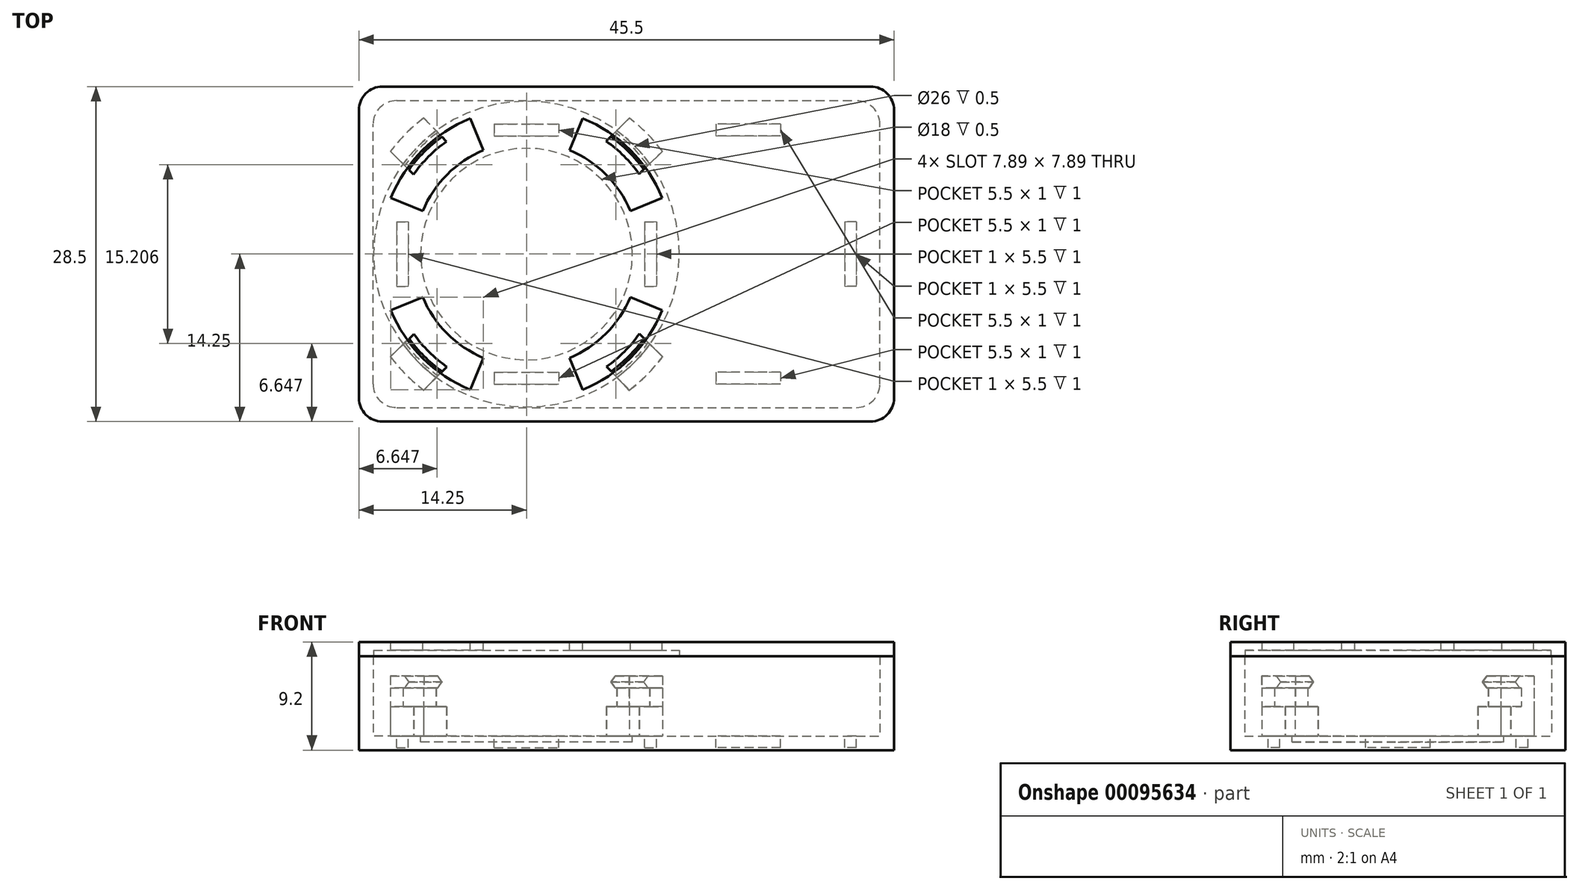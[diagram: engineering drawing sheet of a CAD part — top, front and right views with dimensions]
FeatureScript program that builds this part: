
annotation { "Feature Type Name" : "Feature", "Feature Type Description" : "" }
export const myFeature = defineFeature(function(context is Context, id is Id, definition is map)
    precondition{}
    {
        {
            var Q0;
            Q0=qCreatedBy(makeId("Top.planeOp"),FACE);
            var sketch = newSketch(context, id + "F0", { "sketchPlane" : qUnion([Q0])});
            skLineSegment(sketch, "E0.bottom", {"start": v(0, 0) * mm, "end": v(45.5, 0) * mm});
            skLineSegment(sketch, "E0.top", {"start": v(0, 28.5) * mm, "end": v(45.5, 28.5) * mm});
            skLineSegment(sketch, "E0.left", {"start": v(0, 0) * mm, "end": v(0, 28.5) * mm});
            skLineSegment(sketch, "E0.right", {"start": v(45.5, 0) * mm, "end": v(45.5, 28.5) * mm});
            skSolve(sketch);
        }
        {
            var Q0;
            Q0=qSketchRegion(id+"F0",true);
            extrude(context, id + "F1", {"entities" : qUnion([Q0]), "depth" : 8 * mm});
        }
        {
            var Q0;
            Q0=makeQuery(id+"F1.opExtrude","CAP_FACE",FACE,{"disambiguationData":[OSD([sQuery(id+"F0.wireOp",EDGE,"E0.bottom"),sQuery(id+"F0.wireOp",EDGE,"E0.top"),sQuery(id+"F0.wireOp",EDGE,"E0.left"),sQuery(id+"F0.wireOp",EDGE,"E0.right")])],"isStart":false});
            shell(context, id + "F2", {"entities" : qUnion([Q0]), "thickness" : 1.2 * mm});
        }
        {
            var Q0;
            Q0=makeQuery(id+"F2.opShell","OFFSET_EDGE",EDGE,{"disambiguationData":[OSD([sQuery(id+"F0.wireOp",EDGE,"E0.top"),sQuery(id+"F0.wireOp",EDGE,"E0.right")])]});
            var Q1;
            Q1=makeQuery(id+"F2.opShell","OFFSET_EDGE",EDGE,{"disambiguationData":[OSD([sQuery(id+"F0.wireOp",EDGE,"E0.top"),sQuery(id+"F0.wireOp",EDGE,"E0.left")])]});
            var Q2;
            Q2=makeQuery(id+"F2.opShell","OFFSET_EDGE",EDGE,{"disambiguationData":[OSD([sQuery(id+"F0.wireOp",EDGE,"E0.bottom"),sQuery(id+"F0.wireOp",EDGE,"E0.left")])]});
            var Q3;
            Q3=makeQuery(id+"F1.opExtrude","SWEPT_EDGE",EDGE,{"disambiguationData":[OSD([sQuery(id+"F0.wireOp",EDGE,"E0.top"),sQuery(id+"F0.wireOp",EDGE,"E0.right")])]});
            var Q4;
            Q4=makeQuery(id+"F1.opExtrude","SWEPT_EDGE",EDGE,{"disambiguationData":[OSD([sQuery(id+"F0.wireOp",EDGE,"E0.bottom"),sQuery(id+"F0.wireOp",EDGE,"E0.right")])]});
            var Q5;
            Q5=makeQuery(id+"F1.opExtrude","SWEPT_EDGE",EDGE,{"disambiguationData":[OSD([sQuery(id+"F0.wireOp",EDGE,"E0.top"),sQuery(id+"F0.wireOp",EDGE,"E0.left")])]});
            var Q6;
            Q6=makeQuery(id+"F1.opExtrude","SWEPT_EDGE",EDGE,{"disambiguationData":[OSD([sQuery(id+"F0.wireOp",EDGE,"E0.bottom"),sQuery(id+"F0.wireOp",EDGE,"E0.left")])]});
            var Q7;
            Q7=makeQuery(id+"F2.opShell","OFFSET_EDGE",EDGE,{"disambiguationData":[OSD([sQuery(id+"F0.wireOp",EDGE,"E0.bottom"),sQuery(id+"F0.wireOp",EDGE,"E0.right")])]});
            fillet(context, id + "F3", {"entities" : qUnion([Q0, Q1, Q2, Q3, Q4, Q5, Q6, Q7]), "radius" : 2 * mm, "tangentPropagation" : true, "allowEdgeOverflow" : false});
        }
        {
            var Q0;
            Q0=makeQuery(id+"F1.opExtrude","CAP_FACE",FACE,{"disambiguationData":[OSD([sQuery(id+"F0.wireOp",EDGE,"E0.bottom"),sQuery(id+"F0.wireOp",EDGE,"E0.top"),sQuery(id+"F0.wireOp",EDGE,"E0.left"),sQuery(id+"F0.wireOp",EDGE,"E0.right")])],"isStart":false});
            var sketch = newSketch(context, id + "F4", { "sketchPlane" : qUnion([Q0])});
            skArc(sketch, "E1.0", {"start": v(45.5, 26.5) * mm, "mid": v(44.91, 27.91) * mm, "end": v(43.5, 28.5) * mm});
            skLineSegment(sketch, "E1.1", {"start": v(45.5, 2) * mm, "end": v(45.5, 26.5) * mm});
            skLineSegment(sketch, "E2.0", {"start": v(2, 28.5) * mm, "end": v(43.5, 28.5) * mm});
            skArc(sketch, "E2.1", {"start": v(2, 28.5) * mm, "mid": v(0.59, 27.91) * mm, "end": v(0, 26.5) * mm});
            skArc(sketch, "E2.4", {"start": v(0, 2) * mm, "mid": v(0.59, 0.59) * mm, "end": v(2, 0) * mm});
            skLineSegment(sketch, "E2.5", {"start": v(0, 2) * mm, "end": v(0, 26.5) * mm});
            skArc(sketch, "E3.0", {"start": v(43.5, 0) * mm, "mid": v(44.91, 0.59) * mm, "end": v(45.5, 2) * mm});
            skLineSegment(sketch, "E4", {"start": v(2, 0) * mm, "end": v(43.5, 0) * mm});
            skSolve(sketch);
        }
        {
            var Q0;
            Q0=qSketchRegion(id+"F4",true);
            extrude(context, id + "F5", {"entities" : qUnion([Q0]), "depth" : 1.2 * mm});
        }
        {
            var Q0;
            Q0=makeQuery(id+"F2.opShell","OFFSET_FACE",FACE,{"disambiguationData":[OSD([sQuery(id+"F0.wireOp",EDGE,"E0.bottom"),sQuery(id+"F0.wireOp",EDGE,"E0.top"),sQuery(id+"F0.wireOp",EDGE,"E0.left"),sQuery(id+"F0.wireOp",EDGE,"E0.right")])]});
            var sketch = newSketch(context, id + "F6", { "sketchPlane" : qUnion([Q0])});
            skLineSegment(sketch, "E5.bottom", {"start": v(3.2, 17) * mm, "end": v(4.2, 17) * mm});
            skLineSegment(sketch, "E5.top", {"start": v(3.2, 11.5) * mm, "end": v(4.2, 11.5) * mm});
            skLineSegment(sketch, "E5.left", {"start": v(3.2, 17) * mm, "end": v(3.2, 11.5) * mm});
            skLineSegment(sketch, "E5.right", {"start": v(4.2, 17) * mm, "end": v(4.2, 11.5) * mm});
            skLineSegment(sketch, "E6.bottom", {"start": v(11.5, 25.3) * mm, "end": v(17, 25.3) * mm});
            skLineSegment(sketch, "E6.top", {"start": v(11.5, 24.3) * mm, "end": v(17, 24.3) * mm});
            skLineSegment(sketch, "E6.left", {"start": v(11.5, 25.3) * mm, "end": v(11.5, 24.3) * mm});
            skLineSegment(sketch, "E6.right", {"start": v(17, 25.3) * mm, "end": v(17, 24.3) * mm});
            skLineSegment(sketch, "E7.bottom", {"start": v(11.5, 3.2) * mm, "end": v(17, 3.2) * mm});
            skLineSegment(sketch, "E7.top", {"start": v(11.5, 4.2) * mm, "end": v(17, 4.2) * mm});
            skLineSegment(sketch, "E7.left", {"start": v(11.5, 4.2) * mm, "end": v(11.5, 3.2) * mm});
            skLineSegment(sketch, "E7.right", {"start": v(17, 4.2) * mm, "end": v(17, 3.2) * mm});
            skLineSegment(sketch, "E8.bottom", {"start": v(24.3, 17) * mm, "end": v(25.3, 17) * mm});
            skLineSegment(sketch, "E8.top", {"start": v(24.3, 11.5) * mm, "end": v(25.3, 11.5) * mm});
            skLineSegment(sketch, "E8.left", {"start": v(24.3, 17) * mm, "end": v(24.3, 11.5) * mm});
            skLineSegment(sketch, "E8.right", {"start": v(25.3, 17) * mm, "end": v(25.3, 11.5) * mm});
            skLineSegment(sketch, "E9", {"start": v(14.25, 32.06) * mm, "end": v(14.25, -4.11) * mm, "construction": true});
            skLineSegment(sketch, "E10", {"start": v(0, 14.25) * mm, "end": v(45.5, 14.25) * mm, "construction": true});
            skLineSegment(sketch, "E11", {"start": v(45.5, 14.25) * mm, "end": v(53.48, 14.25) * mm, "construction": true});
            skLineSegment(sketch, "E12.MirrorCS", {"start": v(42.3, 17) * mm, "end": v(41.3, 17) * mm});
            skLineSegment(sketch, "E13.MirrorCS", {"start": v(42.3, 11.5) * mm, "end": v(41.3, 11.5) * mm});
            skLineSegment(sketch, "E14.MirrorCS", {"start": v(30.35, 25.3) * mm, "end": v(30.35, 24.3) * mm});
            skLineSegment(sketch, "E15.MirrorCS", {"start": v(35.85, 4.2) * mm, "end": v(35.85, 3.2) * mm});
            skLineSegment(sketch, "E16.MirrorCS", {"start": v(30.35, 4.2) * mm, "end": v(30.35, 3.2) * mm});
            skLineSegment(sketch, "E17.MirrorCS", {"start": v(35.85, 25.3) * mm, "end": v(35.85, 24.3) * mm});
            skLineSegment(sketch, "E18.MirrorCS", {"start": v(42.3, 17) * mm, "end": v(42.3, 11.5) * mm});
            skLineSegment(sketch, "E19.MirrorCS", {"start": v(41.3, 17) * mm, "end": v(41.3, 11.5) * mm});
            skLineSegment(sketch, "E20.MirrorCS", {"start": v(35.85, 25.3) * mm, "end": v(30.35, 25.3) * mm});
            skLineSegment(sketch, "E21.MirrorCS", {"start": v(35.85, 24.3) * mm, "end": v(30.35, 24.3) * mm});
            skLineSegment(sketch, "E22.MirrorCS", {"start": v(35.85, 4.2) * mm, "end": v(30.35, 4.2) * mm});
            skLineSegment(sketch, "E23.MirrorCS", {"start": v(35.85, 3.2) * mm, "end": v(30.35, 3.2) * mm});
            skSolve(sketch);
        }
        {
            var Q0;
            Q0=qSketchRegion(id+"F6",true);
            extrude(context, id + "F7", {"entities" : qUnion([Q0]), "operationType" : NewBodyOperationType.REMOVE, "oppositeDirection" : true, "depth" : 1 * mm});
        }
        {
            var Q0;
            Q0=makeQuery(id+"F2.opShell","OFFSET_FACE",FACE,{"disambiguationData":[OSD([sQuery(id+"F0.wireOp",EDGE,"E0.bottom"),sQuery(id+"F0.wireOp",EDGE,"E0.top"),sQuery(id+"F0.wireOp",EDGE,"E0.left"),sQuery(id+"F0.wireOp",EDGE,"E0.right")])]});
            var sketch = newSketch(context, id + "F8", { "sketchPlane" : qUnion([Q0])});
            skCircle(sketch, "E24", {"center": v(14.25, 14.25) * mm, "radius": 12.85 * mm, "construction": true});
            skLineSegment(sketch, "E25", {"start": v(14.25, 31.13) * mm, "end": v(14.25, -1.74) * mm, "construction": true});
            skLineSegment(sketch, "E26", {"start": v(14.25, 14.25) * mm, "end": v(3.2, 25.3) * mm, "construction": true});
            skLineSegment(sketch, "E27", {"start": v(4.65, 21.03) * mm, "end": v(2.68, 23) * mm});
            skLineSegment(sketch, "E28", {"start": v(5.51, 25.82) * mm, "end": v(7.44, 23.82) * mm});
            skArc(sketch, "E29.trimOffspring", {"start": v(7.44, 23.82) * mm, "mid": v(5.93, 22.54) * mm, "end": v(4.65, 21.03) * mm});
            skArc(sketch, "E30.trimOffspring", {"start": v(5.51, 25.82) * mm, "mid": v(4, 24.5) * mm, "end": v(2.68, 23) * mm});
            skLineSegment(sketch, "E31.1.0", {"start": v(2.68, 5.51) * mm, "end": v(4.68, 7.44) * mm});
            skArc(sketch, "E31.1.1", {"start": v(2.68, 5.51) * mm, "mid": v(4, 4) * mm, "end": v(5.5, 2.68) * mm});
            skLineSegment(sketch, "E31.1.2", {"start": v(7.47, 4.65) * mm, "end": v(5.5, 2.68) * mm});
            skArc(sketch, "E31.1.3", {"start": v(4.68, 7.44) * mm, "mid": v(5.96, 5.93) * mm, "end": v(7.47, 4.65) * mm});
            skLineSegment(sketch, "E31.2.0", {"start": v(22.99, 2.68) * mm, "end": v(21.06, 4.68) * mm});
            skArc(sketch, "E31.2.1", {"start": v(22.99, 2.68) * mm, "mid": v(24.5, 4) * mm, "end": v(25.82, 5.5) * mm});
            skLineSegment(sketch, "E31.2.2", {"start": v(23.85, 7.47) * mm, "end": v(25.82, 5.5) * mm});
            skArc(sketch, "E31.2.3", {"start": v(21.06, 4.68) * mm, "mid": v(22.57, 5.96) * mm, "end": v(23.85, 7.47) * mm});
            skLineSegment(sketch, "E31.3.0", {"start": v(25.82, 22.99) * mm, "end": v(23.82, 21.06) * mm});
            skArc(sketch, "E31.3.1", {"start": v(25.82, 22.99) * mm, "mid": v(24.5, 24.5) * mm, "end": v(23, 25.82) * mm});
            skLineSegment(sketch, "E31.3.2", {"start": v(21.03, 23.85) * mm, "end": v(23, 25.82) * mm});
            skArc(sketch, "E31.3.3", {"start": v(23.82, 21.06) * mm, "mid": v(22.54, 22.57) * mm, "end": v(21.03, 23.85) * mm});
            skSolve(sketch);
        }
        {
            var Q0;
            Q0=qSketchRegion(id+"F8",true);
            extrude(context, id + "F9", {"entities" : qUnion([Q0]), "operationType" : NewBodyOperationType.ADD, "depth" : 2.5 * mm});
        }
        {
            var Q0;
            Q0=makeQuery(id+"F9.opExtrude","CAP_FACE",FACE,{"disambiguationData":[OSD([sQuery(id+"F8.wireOp",EDGE,"E27"),sQuery(id+"F8.wireOp",EDGE,"E28"),sQuery(id+"F8.wireOp",EDGE,"E29.trimOffspring"),sQuery(id+"F8.wireOp",EDGE,"E30.trimOffspring")])],"isStart":false});
            var sketch = newSketch(context, id + "F10", { "sketchPlane" : qUnion([Q0])});
            skArc(sketch, "E32", {"start": v(3.75, 6.58) * mm, "mid": v(5.06, 5.06) * mm, "end": v(6.58, 3.75) * mm});
            skArc(sketch, "E33", {"start": v(5.51, 25.82) * mm, "mid": v(4, 24.5) * mm, "end": v(2.68, 23) * mm});
            skLineSegment(sketch, "E34", {"start": v(6.56, 24.73) * mm, "end": v(5.51, 25.82) * mm});
            skLineSegment(sketch, "E35", {"start": v(3.75, 21.92) * mm, "end": v(2.68, 23) * mm});
            skLineSegment(sketch, "E36", {"start": v(22.99, 25.82) * mm, "end": v(21.92, 24.75) * mm});
            skLineSegment(sketch, "E37", {"start": v(24.72, 21.96) * mm, "end": v(25.82, 22.99) * mm});
            skLineSegment(sketch, "E38", {"start": v(24.75, 6.58) * mm, "end": v(25.82, 5.51) * mm});
            skLineSegment(sketch, "E39", {"start": v(21.94, 3.77) * mm, "end": v(22.98, 2.67) * mm});
            skLineSegment(sketch, "E40", {"start": v(3.75, 6.58) * mm, "end": v(2.67, 5.52) * mm});
            skLineSegment(sketch, "E41", {"start": v(5.5, 2.68) * mm, "end": v(6.58, 3.75) * mm});
            skArc(sketch, "E42.trimOffspring", {"start": v(6.56, 24.73) * mm, "mid": v(5.05, 23.43) * mm, "end": v(3.75, 21.92) * mm});
            skArc(sketch, "E43.trimOffspring", {"start": v(2.67, 5.52) * mm, "mid": v(3.99, 4) * mm, "end": v(5.5, 2.68) * mm});
            skArc(sketch, "E44.trimOffspring", {"start": v(22.98, 2.67) * mm, "mid": v(24.5, 4) * mm, "end": v(25.82, 5.51) * mm});
            skArc(sketch, "E45.trimOffspring", {"start": v(25.82, 22.99) * mm, "mid": v(24.5, 24.5) * mm, "end": v(22.99, 25.82) * mm});
            skArc(sketch, "E46.trimOffspring", {"start": v(24.72, 21.96) * mm, "mid": v(23.43, 23.46) * mm, "end": v(21.92, 24.75) * mm});
            skArc(sketch, "E47.trimOffspring", {"start": v(21.94, 3.77) * mm, "mid": v(23.45, 5.07) * mm, "end": v(24.75, 6.58) * mm});
            skSolve(sketch);
        }
        {
            var Q0;
            Q0=qSketchRegion(id+"F10",true);
            extrude(context, id + "F11", {"entities" : qUnion([Q0]), "operationType" : NewBodyOperationType.ADD, "depth" : 1.6 * mm});
        }
        {
            var Q0;
            Q0=makeQuery(id+"F11.opExtrude","CAP_FACE",FACE,{"disambiguationData":[OSD([sQuery(id+"F10.wireOp",EDGE,"E36"),sQuery(id+"F10.wireOp",EDGE,"E37"),sQuery(id+"F10.wireOp",EDGE,"E45.trimOffspring"),sQuery(id+"F10.wireOp",EDGE,"E46.trimOffspring")])],"isStart":false});
            var sketch = newSketch(context, id + "F12", { "sketchPlane" : qUnion([Q0])});
            skArc(sketch, "E48", {"start": v(7.05, 24.23) * mm, "mid": v(5.54, 22.93) * mm, "end": v(4.25, 21.42) * mm});
            skArc(sketch, "E49", {"start": v(5.52, 25.82) * mm, "mid": v(4, 24.5) * mm, "end": v(2.68, 22.99) * mm});
            skLineSegment(sketch, "E50", {"start": v(22.99, 25.82) * mm, "end": v(21.42, 24.24) * mm});
            skLineSegment(sketch, "E51", {"start": v(25.82, 22.99) * mm, "end": v(24.2, 21.47) * mm});
            skLineSegment(sketch, "E52", {"start": v(24.2, 21.47) * mm, "end": v(24.19, 21.46) * mm});
            skLineSegment(sketch, "E53", {"start": v(5.52, 25.82) * mm, "end": v(7.05, 24.23) * mm});
            skLineSegment(sketch, "E54", {"start": v(2.68, 22.99) * mm, "end": v(4.25, 21.42) * mm});
            skLineSegment(sketch, "E55", {"start": v(2.67, 5.53) * mm, "end": v(4.25, 7.08) * mm});
            skLineSegment(sketch, "E56", {"start": v(5.52, 2.67) * mm, "end": v(7.04, 4.28) * mm});
            skLineSegment(sketch, "E57", {"start": v(25.83, 5.53) * mm, "end": v(24.22, 7.05) * mm});
            skLineSegment(sketch, "E58", {"start": v(22.96, 2.66) * mm, "end": v(21.45, 4.28) * mm});
            skArc(sketch, "E59.trimOffspring", {"start": v(4.25, 7.08) * mm, "mid": v(5.53, 5.57) * mm, "end": v(7.04, 4.28) * mm});
            skArc(sketch, "E60.trimOffspring", {"start": v(2.67, 5.53) * mm, "mid": v(4, 4) * mm, "end": v(5.52, 2.67) * mm});
            skArc(sketch, "E61.trimOffspring", {"start": v(24.2, 21.47) * mm, "mid": v(22.92, 22.97) * mm, "end": v(21.42, 24.24) * mm});
            skArc(sketch, "E62.trimOffspring", {"start": v(25.82, 22.99) * mm, "mid": v(24.5, 24.5) * mm, "end": v(22.99, 25.82) * mm});
            skArc(sketch, "E63.trimOffspring", {"start": v(21.45, 4.28) * mm, "mid": v(22.95, 5.55) * mm, "end": v(24.22, 7.05) * mm});
            skArc(sketch, "E64.trimOffspring", {"start": v(22.96, 2.66) * mm, "mid": v(24.5, 4) * mm, "end": v(25.83, 5.53) * mm});
            skSolve(sketch);
        }
        {
            var Q0;
            Q0=qSketchRegion(id+"F12",true);
            extrude(context, id + "F13", {"entities" : qUnion([Q0]), "operationType" : NewBodyOperationType.ADD, "depth" : 1 * mm});
        }
        {
            var Q0;
            Q0=makeQuery(id+"F13.opExtrude","CAP_EDGE",EDGE,{"disambiguationData":[OSD([sQuery(id+"F12.wireOp",EDGE,"E59.trimOffspring")])],"isStart":false});
            var Q1;
            Q1=makeQuery(id+"F13.opExtrude","CAP_EDGE",EDGE,{"disambiguationData":[OSD([sQuery(id+"F12.wireOp",EDGE,"E59.trimOffspring")])],"isStart":true});
            var Q2;
            Q2=makeQuery(id+"F13.opExtrude","CAP_EDGE",EDGE,{"disambiguationData":[OSD([sQuery(id+"F12.wireOp",EDGE,"E48")])],"isStart":false});
            var Q3;
            Q3=makeQuery(id+"F13.opExtrude","CAP_EDGE",EDGE,{"disambiguationData":[OSD([sQuery(id+"F12.wireOp",EDGE,"E48")])],"isStart":true});
            var Q4;
            Q4=makeQuery(id+"F13.opExtrude","CAP_EDGE",EDGE,{"disambiguationData":[OSD([sQuery(id+"F12.wireOp",EDGE,"E61.trimOffspring")])],"isStart":false});
            var Q5;
            Q5=makeQuery(id+"F13.opExtrude","CAP_EDGE",EDGE,{"disambiguationData":[OSD([sQuery(id+"F12.wireOp",EDGE,"E63.trimOffspring")])],"isStart":false});
            var Q6;
            Q6=makeQuery(id+"F13.opExtrude","CAP_EDGE",EDGE,{"disambiguationData":[OSD([sQuery(id+"F12.wireOp",EDGE,"E63.trimOffspring")])],"isStart":true});
            var Q7;
            Q7=makeQuery(id+"F13.opExtrude","CAP_EDGE",EDGE,{"disambiguationData":[OSD([sQuery(id+"F12.wireOp",EDGE,"E61.trimOffspring")])],"isStart":true});
            chamfer(context, id + "F14", {"entities" : qUnion([Q0, Q1, Q2, Q3, Q4, Q5, Q6, Q7]), "width" : .5 * mm, "tangentPropagation" : true});
        }
        {
            var Q0;
            Q0=makeQuery(id+"F2.opShell","OFFSET_FACE",FACE,{"disambiguationData":[OSD([sQuery(id+"F0.wireOp",EDGE,"E0.bottom"),sQuery(id+"F0.wireOp",EDGE,"E0.top"),sQuery(id+"F0.wireOp",EDGE,"E0.left"),sQuery(id+"F0.wireOp",EDGE,"E0.right")])]});
            var sketch = newSketch(context, id + "F15", { "sketchPlane" : qUnion([Q0])});
            skCircle(sketch, "E65", {"center": v(14.25, 14.25) * mm, "radius": 9 * mm});
            skSolve(sketch);
        }
        {
            var Q0;
            Q0=qSketchRegion(id+"F15",true);
            extrude(context, id + "F16", {"entities" : qUnion([Q0]), "operationType" : NewBodyOperationType.REMOVE, "oppositeDirection" : true, "depth" : .5 * mm});
        }
        {
            var Q0;
            Q0=makeQuery(id+"F5.opExtrude","CAP_FACE",FACE,{"disambiguationData":[OSD([sQuery(id+"F4.wireOp",EDGE,"E1.0"),sQuery(id+"F4.wireOp",EDGE,"E1.1"),sQuery(id+"F4.wireOp",EDGE,"E2.0"),sQuery(id+"F4.wireOp",EDGE,"E2.1"),sQuery(id+"F4.wireOp",EDGE,"E2.4"),sQuery(id+"F4.wireOp",EDGE,"E2.5"),sQuery(id+"F4.wireOp",EDGE,"E3.0"),sQuery(id+"F4.wireOp",EDGE,"E4")])],"isStart":false});
            var sketch = newSketch(context, id + "F17", { "sketchPlane" : qUnion([Q0])});
            skArc(sketch, "E66", {"start": v(2.7, 9.47) * mm, "mid": v(5.41, 5.41) * mm, "end": v(9.47, 2.7) * mm});
            skArc(sketch, "E67", {"start": v(5.42, 10.6) * mm, "mid": v(7.5, 7.5) * mm, "end": v(10.6, 5.42) * mm});
            skLineSegment(sketch, "E68", {"start": v(17.9, 23.08) * mm, "end": v(19.03, 25.8) * mm});
            skLineSegment(sketch, "E69", {"start": v(23.08, 17.9) * mm, "end": v(25.8, 19.03) * mm});
            skLineSegment(sketch, "E70", {"start": v(14.25, 14.25) * mm, "end": v(27.9, 27.9) * mm, "construction": true});
            skLineSegment(sketch, "E71", {"start": v(14.25, 14.25) * mm, "end": v(14.25, 29.28) * mm, "construction": true});
            skLineSegment(sketch, "E72", {"start": v(14.25, 14.25) * mm, "end": v(1.2, 27.3) * mm, "construction": true});
            skLineSegment(sketch, "E73", {"start": v(14.25, 14.25) * mm, "end": v(6, 6) * mm, "construction": true});
            skLineSegment(sketch, "E74", {"start": v(14.25, 14.25) * mm, "end": v(24.15, 4.35) * mm, "construction": true});
            skLineSegment(sketch, "E75", {"start": v(10.6, 23.08) * mm, "end": v(9.47, 25.8) * mm});
            skLineSegment(sketch, "E76", {"start": v(5.42, 17.9) * mm, "end": v(2.7, 19.03) * mm});
            skLineSegment(sketch, "E77", {"start": v(5.42, 10.6) * mm, "end": v(2.7, 9.47) * mm});
            skLineSegment(sketch, "E78", {"start": v(10.6, 5.42) * mm, "end": v(9.47, 2.7) * mm});
            skLineSegment(sketch, "E79", {"start": v(17.9, 5.42) * mm, "end": v(19.03, 2.7) * mm});
            skLineSegment(sketch, "E80", {"start": v(23.08, 10.6) * mm, "end": v(25.8, 9.47) * mm});
            skArc(sketch, "E81.trimOffspring", {"start": v(23.08, 17.9) * mm, "mid": v(21, 21) * mm, "end": v(17.9, 23.08) * mm});
            skArc(sketch, "E82.trimOffspring", {"start": v(25.8, 19.03) * mm, "mid": v(23.09, 23.09) * mm, "end": v(19.03, 25.8) * mm});
            skArc(sketch, "E83.trimOffspring", {"start": v(10.6, 23.08) * mm, "mid": v(7.5, 21) * mm, "end": v(5.42, 17.9) * mm});
            skArc(sketch, "E84.trimOffspring", {"start": v(9.47, 25.8) * mm, "mid": v(5.41, 23.09) * mm, "end": v(2.7, 19.03) * mm});
            skArc(sketch, "E85.trimOffspring", {"start": v(17.9, 5.42) * mm, "mid": v(21, 7.5) * mm, "end": v(23.08, 10.6) * mm});
            skArc(sketch, "E86.trimOffspring", {"start": v(19.03, 2.7) * mm, "mid": v(23.09, 5.41) * mm, "end": v(25.8, 9.47) * mm});
            skSolve(sketch);
        }
        {
            var Q0;
            Q0=makeQuery(id+"F17.imprint","IMPRINT",FACE,{"disambiguationData":[TD([[makeQuery(id+"F17.imprint","IMPRINT",EDGE,{"derivedFrom":sQuery(id+"F17.wireOp",EDGE,"E66")}),1.0]])]});
            var Q1;
            Q1=makeQuery(id+"F17.imprint","IMPRINT",FACE,{"disambiguationData":[TD([[makeQuery(id+"F17.imprint","IMPRINT",EDGE,{"derivedFrom":sQuery(id+"F17.wireOp",EDGE,"E68")}),-1.0]])]});
            var Q2;
            Q2=makeQuery(id+"F17.imprint","IMPRINT",FACE,{"disambiguationData":[TD([[makeQuery(id+"F17.imprint","IMPRINT",EDGE,{"derivedFrom":sQuery(id+"F17.wireOp",EDGE,"E75")}),1.0]])]});
            var Q3;
            Q3=makeQuery(id+"F17.imprint","IMPRINT",FACE,{"disambiguationData":[TD([[makeQuery(id+"F17.imprint","IMPRINT",EDGE,{"derivedFrom":sQuery(id+"F17.wireOp",EDGE,"E79")}),1.0]])]});
            extrude(context, id + "F18", {"entities" : qUnion([Q0, Q1, Q2, Q3]), "operationType" : NewBodyOperationType.REMOVE, "oppositeDirection" : true, "depth" : 2 * mm});
        }
        {
            var Q0;
            Q0=makeQuery(id+"F5.opExtrude","CAP_FACE",FACE,{"disambiguationData":[OSD([sQuery(id+"F4.wireOp",EDGE,"E1.0"),sQuery(id+"F4.wireOp",EDGE,"E1.1"),sQuery(id+"F4.wireOp",EDGE,"E2.0"),sQuery(id+"F4.wireOp",EDGE,"E2.1"),sQuery(id+"F4.wireOp",EDGE,"E2.4"),sQuery(id+"F4.wireOp",EDGE,"E2.5"),sQuery(id+"F4.wireOp",EDGE,"E3.0"),sQuery(id+"F4.wireOp",EDGE,"E4")])],"isStart":true});
            var sketch = newSketch(context, id + "F19", { "sketchPlane" : qUnion([Q0])});
            skCircle(sketch, "E87", {"center": v(14.25, -14.25) * mm, "radius": 13 * mm});
            skSolve(sketch);
        }
        {
            var Q0;
            {var subQ1=makeQuery(id+"F5.opExtrude","CAP_FACE",FACE,{"disambiguationData":[OSD([sQuery(id+"F4.wireOp",EDGE,"E1.0"),sQuery(id+"F4.wireOp",EDGE,"E1.1"),sQuery(id+"F4.wireOp",EDGE,"E2.0"),sQuery(id+"F4.wireOp",EDGE,"E2.1"),sQuery(id+"F4.wireOp",EDGE,"E2.4"),sQuery(id+"F4.wireOp",EDGE,"E2.5"),sQuery(id+"F4.wireOp",EDGE,"E3.0"),sQuery(id+"F4.wireOp",EDGE,"E4")])],"isStart":true});var subQ2=makeQuery(id+"F18.boolean.opBoolean","INTERSECT",EDGE,{"derivedFrom":[subQ1,makeQuery(id+"F18.opExtrude","SWEPT_FACE",FACE,{"disambiguationData":[OSD([sQuery(id+"F17.wireOp",EDGE,"E68")])]})]});Q0=makeQuery(id+"F19.imprint","IMPRINT",FACE,{"disambiguationData":[TD([[makeQuery(id+"F19.imprint","IMPRINT",EDGE,{"derivedFrom":subQ2}),1.0]])]});}
            var Q1;
            {var subQ1=makeQuery(id+"F5.opExtrude","CAP_FACE",FACE,{"disambiguationData":[OSD([sQuery(id+"F4.wireOp",EDGE,"E1.0"),sQuery(id+"F4.wireOp",EDGE,"E1.1"),sQuery(id+"F4.wireOp",EDGE,"E2.0"),sQuery(id+"F4.wireOp",EDGE,"E2.1"),sQuery(id+"F4.wireOp",EDGE,"E2.4"),sQuery(id+"F4.wireOp",EDGE,"E2.5"),sQuery(id+"F4.wireOp",EDGE,"E3.0"),sQuery(id+"F4.wireOp",EDGE,"E4")])],"isStart":true});var subQ2=makeQuery(id+"F18.boolean.opBoolean","INTERSECT",EDGE,{"derivedFrom":[subQ1,makeQuery(id+"F18.opExtrude","SWEPT_FACE",FACE,{"disambiguationData":[OSD([sQuery(id+"F17.wireOp",EDGE,"E75")])]})]});Q1=makeQuery(id+"F19.imprint","IMPRINT",FACE,{"disambiguationData":[TD([[makeQuery(id+"F19.imprint","IMPRINT",EDGE,{"derivedFrom":subQ2}),-1.0]])]});}
            var Q2;
            {var subQ1=makeQuery(id+"F5.opExtrude","CAP_FACE",FACE,{"disambiguationData":[OSD([sQuery(id+"F4.wireOp",EDGE,"E1.0"),sQuery(id+"F4.wireOp",EDGE,"E1.1"),sQuery(id+"F4.wireOp",EDGE,"E2.0"),sQuery(id+"F4.wireOp",EDGE,"E2.1"),sQuery(id+"F4.wireOp",EDGE,"E2.4"),sQuery(id+"F4.wireOp",EDGE,"E2.5"),sQuery(id+"F4.wireOp",EDGE,"E3.0"),sQuery(id+"F4.wireOp",EDGE,"E4")])],"isStart":true});Q2=makeQuery(id+"F19.imprint","IMPRINT",FACE,{"disambiguationData":[TD([[makeQuery(id+"F19.imprint","IMPRINT",EDGE,{"derivedFrom":makeQuery(id+"F18.boolean.opBoolean","INTERSECT",EDGE,{"derivedFrom":[subQ1,makeQuery(id+"F18.opExtrude","SWEPT_FACE",FACE,{"disambiguationData":[OSD([sQuery(id+"F17.wireOp",EDGE,"E67")])]})]})}),1.0]])]});}
            var Q3;
            {var subQ1=makeQuery(id+"F5.opExtrude","CAP_FACE",FACE,{"disambiguationData":[OSD([sQuery(id+"F4.wireOp",EDGE,"E1.0"),sQuery(id+"F4.wireOp",EDGE,"E1.1"),sQuery(id+"F4.wireOp",EDGE,"E2.0"),sQuery(id+"F4.wireOp",EDGE,"E2.1"),sQuery(id+"F4.wireOp",EDGE,"E2.4"),sQuery(id+"F4.wireOp",EDGE,"E2.5"),sQuery(id+"F4.wireOp",EDGE,"E3.0"),sQuery(id+"F4.wireOp",EDGE,"E4")])],"isStart":true});var subQ2=makeQuery(id+"F18.boolean.opBoolean","INTERSECT",EDGE,{"derivedFrom":[subQ1,makeQuery(id+"F18.opExtrude","SWEPT_FACE",FACE,{"disambiguationData":[OSD([sQuery(id+"F17.wireOp",EDGE,"E79")])]})]});Q3=makeQuery(id+"F19.imprint","IMPRINT",FACE,{"disambiguationData":[TD([[makeQuery(id+"F19.imprint","IMPRINT",EDGE,{"derivedFrom":subQ2}),-1.0]])]});}
            var Q4;
            {var subQ0=makeQuery(id+"F5.opExtrude","CAP_FACE",FACE,{"disambiguationData":[OSD([sQuery(id+"F4.wireOp",EDGE,"E1.0"),sQuery(id+"F4.wireOp",EDGE,"E1.1"),sQuery(id+"F4.wireOp",EDGE,"E2.0"),sQuery(id+"F4.wireOp",EDGE,"E2.1"),sQuery(id+"F4.wireOp",EDGE,"E2.4"),sQuery(id+"F4.wireOp",EDGE,"E2.5"),sQuery(id+"F4.wireOp",EDGE,"E3.0"),sQuery(id+"F4.wireOp",EDGE,"E4")])],"isStart":true});Q4=makeQuery(id+"F19.imprint","IMPRINT",FACE,{"disambiguationData":[TD([[makeQuery(id+"F19.imprint","IMPRINT",EDGE,{"derivedFrom":makeQuery(id+"F18.boolean.opBoolean","INTERSECT",EDGE,{"derivedFrom":[subQ0,makeQuery(id+"F18.opExtrude","SWEPT_FACE",FACE,{"disambiguationData":[OSD([sQuery(id+"F17.wireOp",EDGE,"E67")])]})]})}),-1.0]])]});}
            extrude(context, id + "F20", {"entities" : qUnion([Q0, Q1, Q2, Q3, Q4]), "operationType" : NewBodyOperationType.REMOVE, "oppositeDirection" : true, "depth" : 0.5 * mm});
        }
    });
